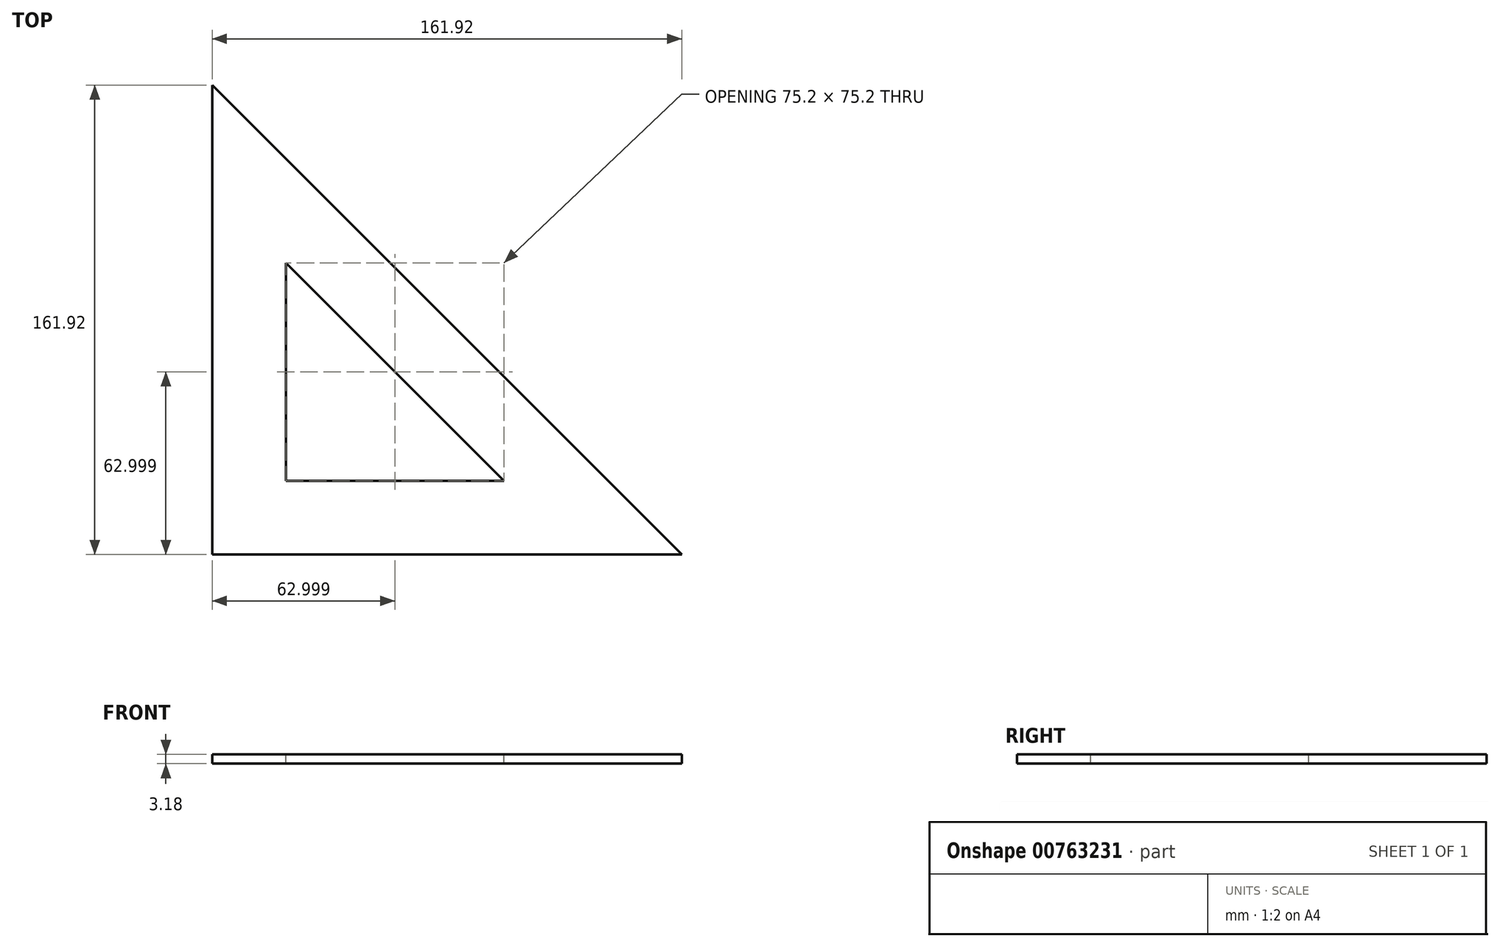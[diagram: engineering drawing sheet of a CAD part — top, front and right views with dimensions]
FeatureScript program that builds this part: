
annotation { "Feature Type Name" : "Feature", "Feature Type Description" : "" }
export const myFeature = defineFeature(function(context is Context, id is Id, definition is map)
    precondition{}
    {
        {
            var Q0;
            Q0=qCreatedBy(makeId("Top.planeOp"),FACE);
            var sketch = newSketch(context, id + "F0", { "sketchPlane" : qUnion([Q0])});
            skLineSegment(sketch, "E0.top", {"start": v(80.96, -80.96) * mm, "end": v(-80.96, -80.96) * mm});
            skLineSegment(sketch, "E0.right", {"start": v(-80.96, 80.96) * mm, "end": v(-80.96, -80.96) * mm});
            skPoint(sketch, "E0.middle", {"position": v(0, 0) * mm});
            skLineSegment(sketch, "E1", {"start": v(-80.96, 80.96) * mm, "end": v(80.96, -80.96) * mm});
            skSolve(sketch);
        }
        {
            var Q0;
            Q0=makeQuery(id+"F0.imprint","IMPRINT",FACE,{"disambiguationData":[TD([[makeQuery(id+"F0.imprint","IMPRINT",EDGE,{"derivedFrom":sQuery(id+"F0.wireOp",EDGE,"E0.top")}),-1.0]])]});
            extrude(context, id + "F1", {"entities" : qUnion([Q0]), "endBound" : BoundingType.SYMMETRIC, "depth" : 3.17 * mm, "offsetDistance" : 25.4 * mm});
        }
        {
            var Q0;
            Q0=makeQuery(id+"F1.opExtrude","CAP_FACE",FACE,{"disambiguationData":[OSD([sQuery(id+"F0.wireOp",EDGE,"E0.top"),sQuery(id+"F0.wireOp",EDGE,"E0.right"),sQuery(id+"F0.wireOp",EDGE,"E1")])],"isStart":false});
            var sketch = newSketch(context, id + "F2", { "sketchPlane" : qUnion([Q0])});
            skLineSegment(sketch, "E2", {"start": v(-55.56, 19.64) * mm, "end": v(-55.56, -55.56) * mm});
            skLineSegment(sketch, "E3", {"start": v(-55.56, -55.56) * mm, "end": v(19.64, -55.56) * mm});
            skLineSegment(sketch, "E4", {"start": v(19.64, -55.56) * mm, "end": v(-55.56, 19.64) * mm});
            skSolve(sketch);
        }
        {
            var Q0;
            Q0=makeQuery(id+"F2.imprint","IMPRINT",FACE,{"disambiguationData":[TD([[makeQuery(id+"F2.imprint","IMPRINT",EDGE,{"derivedFrom":sQuery(id+"F2.wireOp",EDGE,"E2")}),1.0]])]});
            extrude(context, id + "F3", {"entities" : qUnion([Q0]), "operationType" : NewBodyOperationType.REMOVE, "endBound" : BoundingType.THROUGH_ALL, "oppositeDirection" : true, "depth" : 25.4 * mm, "offsetDistance" : 25.4 * mm});
        }
    });
